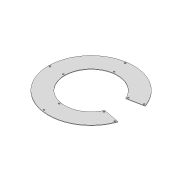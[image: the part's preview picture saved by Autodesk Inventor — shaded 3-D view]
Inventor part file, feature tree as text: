
AUTODESK INVENTOR PART (.ipt)
format: ipt  version: 2021 (Build 250183000, 183)  size: 121,344 bytes
history: native  units: mm
features: extrude x1, sketch x1
ambient origin geometry x8: Origin, YZ Plane, XZ Plane, XY Plane, X Axis, Y Axis, Z Axis, Center Point
bodies: Solid1 (feature_tree)
feature tree (2):
  extrude  "Extrusion1"  Depth=7.0mm
  sketch  "Sketch1"  dims[d0=504.787567mm d1=944.787567mm d34=1152.87mm d48=712.87mm d52=20.0mm d53=20.0mm d54=376.435mm d55=20.0mm d56=20.0mm d58=556.435mm d59=20.0mm d60=376.435mm d61=20.0mm d62=556.435mm d63=20.0mm d65=14.137167mm d67=20.0mm d69=14.137167mm d71=7.0mm d72=0.0mm]
